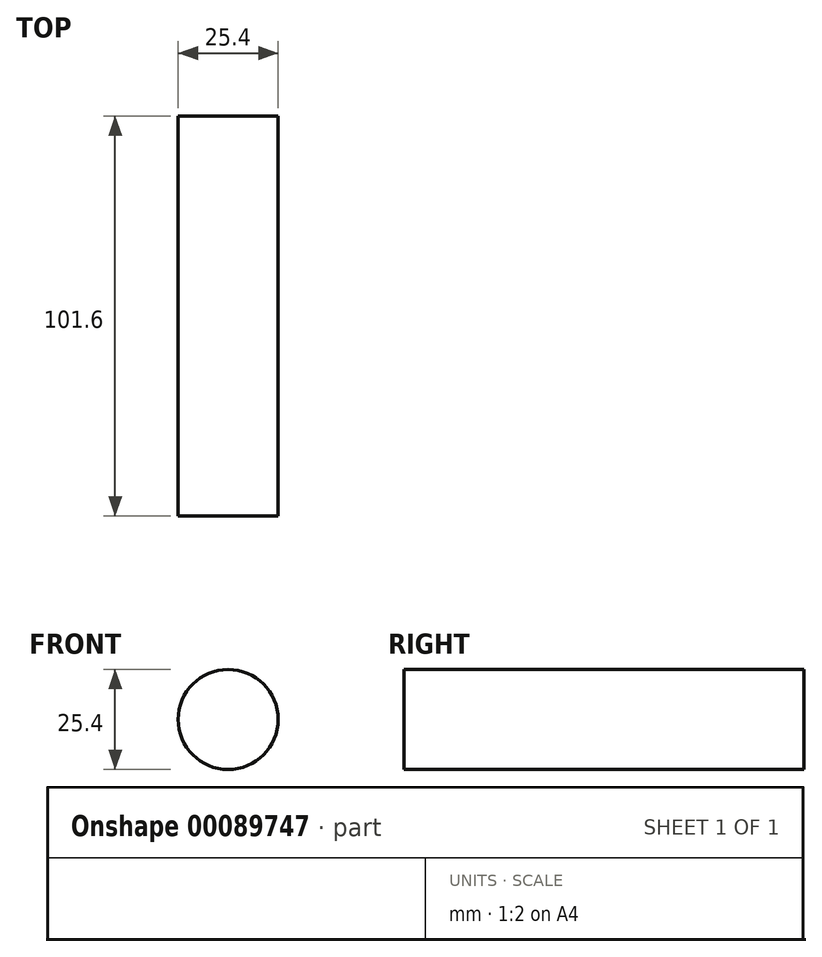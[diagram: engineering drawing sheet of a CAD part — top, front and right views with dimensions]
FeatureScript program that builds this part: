
annotation { "Feature Type Name" : "Feature", "Feature Type Description" : "" }
export const myFeature = defineFeature(function(context is Context, id is Id, definition is map)
    precondition{}
    {
        {
            var Q0;
            Q0=qCreatedBy(makeId("Front.planeOp"),FACE);
            var sketch = newSketch(context, id + "F0", { "sketchPlane" : qUnion([Q0])});
            skCircle(sketch, "E0", {"center": v(0, 0) * mm, "radius": 12.7 * mm});
            skSolve(sketch);
        }
        {
            var Q0;
            Q0 = qSketchRegion(id + "F0", true);
            extrude(context, id + "F1", {"entities" : qUnion([Q0]), "depth" : 101.6 * mm});
        }
    });
